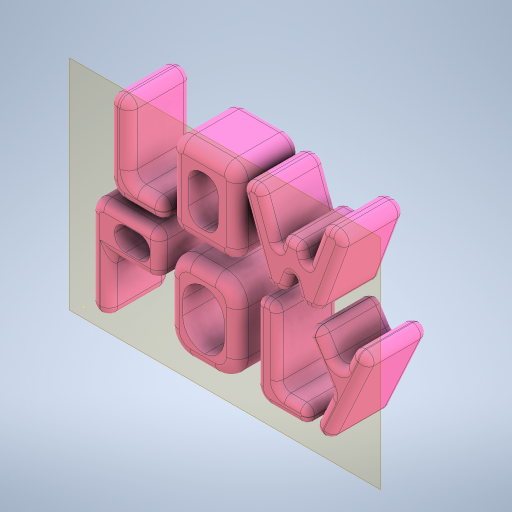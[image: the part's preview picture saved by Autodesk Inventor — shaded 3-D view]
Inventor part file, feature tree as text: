
AUTODESK INVENTOR PART (.ipt)
format: ipt  version: 2024.1 (Build 281209000, 209)  size: 945,152 bytes
history: native  units: mm
features: fillet x23, sketch x4, extrude x3, projected_geometry x1
ambient origin geometry x8: Origin, YZ Plane, XZ Plane, XY Plane, X Axis, Y Axis, Z Axis, Center Point
bodies: Solid2 (feature_tree)
feature tree (31):
  extrude  "Extrusion6"  Depth=10.0mm TaperAngle=0.0deg
  extrude  "Extrusion1"  Depth=90.0mm
  extrude  "Extrusion7"  Depth=1.0mm
  fillet  "Fillet1"  Radius=19.198622mm
  fillet  "Fillet2"  Radius=10.0mm
  fillet  "Fillet3"  Radius=28.0mm
  fillet  "Fillet4"  [1 undecoded]
  fillet  "Fillet5"  Radius=4.0mm
  fillet  "Fillet6"  Radius=5.0mm
  fillet  "Fillet7"  Radius=5.0mm
  fillet  "Fillet8"  Radius=10.0mm
  fillet  "Fillet9"  Radius=10.0mm
  fillet  "Fillet10"  Radius=5.0mm
  fillet  "Fillet11"  Radius=3.5mm
  fillet  "Fillet12"  Radius=3.0mm
  fillet  "Fillet13"  Radius=6.0mm
  fillet  "Fillet14"  Radius=3.5mm
  fillet  "Fillet15"  Radius=3.5mm
  fillet  "Fillet16"  Radius=4.0mm
  fillet  "Fillet17"  Radius=4.0mm
  fillet  "Fillet18"  Radius=7.0mm
  fillet  "Fillet19"  Radius=6.0mm
  fillet  "Fillet20"  Radius=6.0mm
  fillet  "Fillet21"  Radius=5.0mm
  fillet  "Fillet22"  Radius=4.0mm
  fillet  "Fillet23"  Radius=1.0mm
  sketch  "Sketch8"  dims[d61=3.0mm d62=3.0mm d63=19.198622mm d64=7.056118mm d65=7.5mm d66=6.0mm d67=3.0mm d69=3.931055mm d70=3.9mm]
  sketch  "Sketch1"  dims[d0=40.0mm d4=10.0mm d5=0.0mm]
  sketch  "Sketch6"  dims[d24=160.0mm d25=90.0mm]
  projected_geometry  "Projected Loop1"
  sketch  "Sketch7"  dims[d26=90.0mm d27=0.0mm d28=19.198622mm d29=19.198622mm d31=10.0mm d39=28.0mm d40=0.0mm d41=0.0mm d42=4.0mm d43=5.0mm d44=5.0mm d45=10.0mm d46=10.0mm d47=5.0mm d48=3.5mm d49=3.0mm d50=6.0mm d51=3.5mm d52=3.5mm d53=4.0mm d54=4.0mm d55=7.0mm d56=6.0mm d57=6.0mm d58=5.0mm d59=4.0mm d60=1.0mm]
note: 1 required parameter value undecoded (feature->parameter linkage not recoverable at this tier; creation-order binding heuristic only, values carry confidence <= 0.55)
